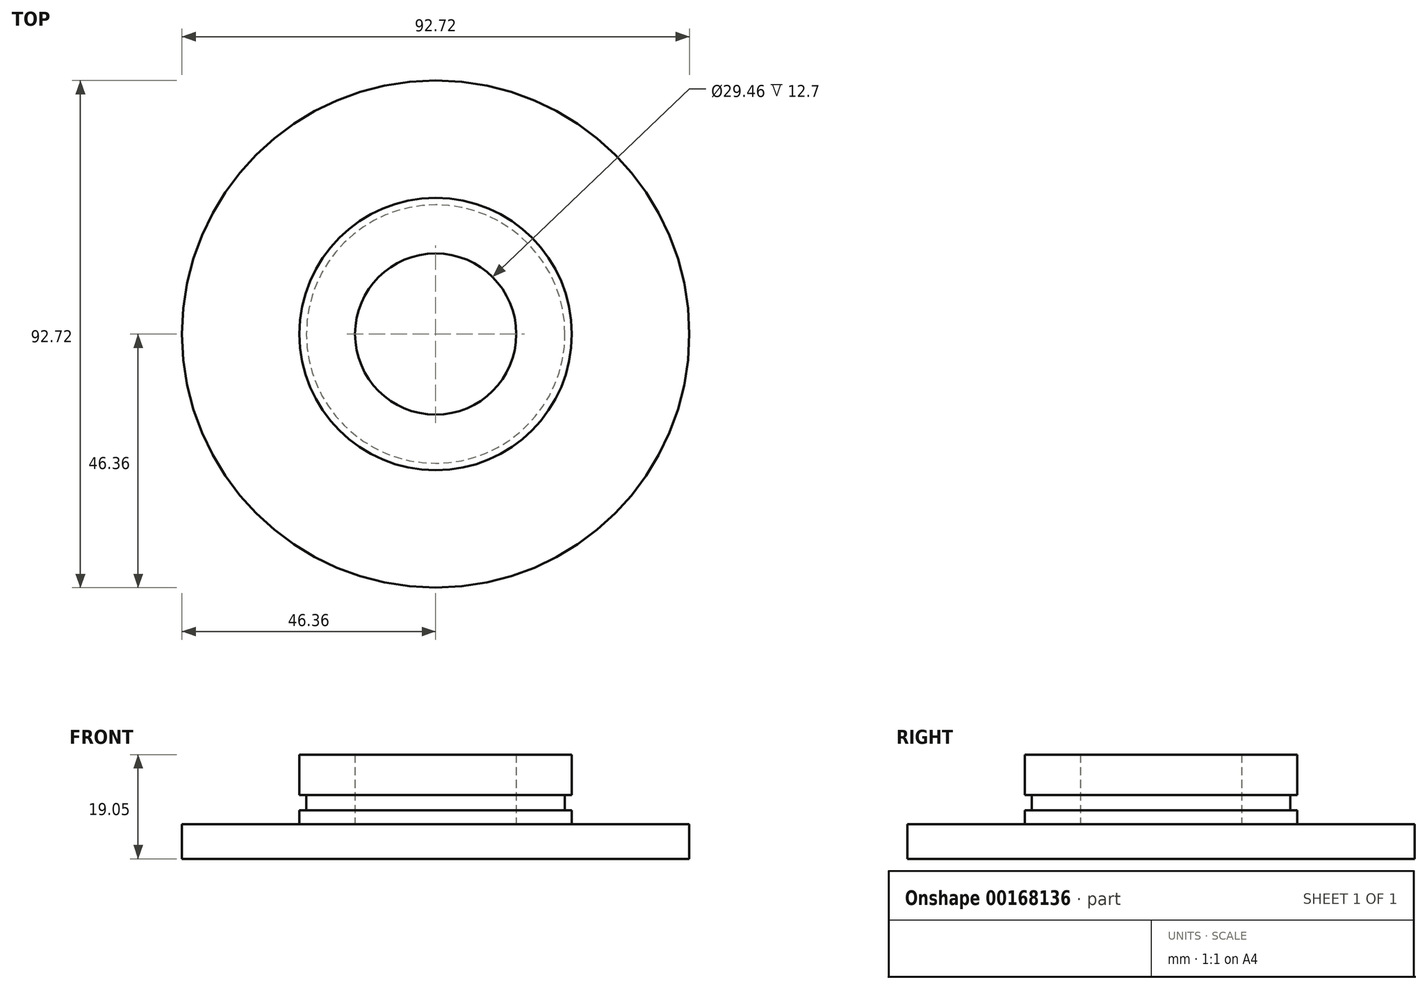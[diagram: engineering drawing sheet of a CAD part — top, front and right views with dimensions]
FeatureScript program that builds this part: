
annotation { "Feature Type Name" : "Feature", "Feature Type Description" : "" }
export const myFeature = defineFeature(function(context is Context, id is Id, definition is map)
    precondition{}
    {
        {
            var Q0;
            Q0=qCreatedBy(makeId("Top.planeOp"),FACE);
            var sketch = newSketch(context, id + "F0", { "sketchPlane" : qUnion([Q0])});
            skCircle(sketch, "E0", {"center": v(0, 0) * mm, "radius": 46.35 * mm});
            skSolve(sketch);
        }
        {
            var Q0;
            Q0=makeQuery(id+"F0.imprint","IMPRINT",FACE,{"disambiguationData":[TD([[makeQuery(id+"F0.imprint","IMPRINT",EDGE,{"derivedFrom":sQuery(id+"F0.wireOp",EDGE,"E0")}),1.0]])]});
            extrude(context, id + "F1", {"entities" : qUnion([Q0]), "depth" : 6.35 * mm});
        }
        {
            var Q0;
            Q0=makeQuery(id+"F1.opExtrude","CAP_FACE",FACE,{"disambiguationData":[OSD([sQuery(id+"F0.wireOp",EDGE,"E0")])],"isStart":false});
            var sketch = newSketch(context, id + "F2", { "sketchPlane" : qUnion([Q0])});
            skCircle(sketch, "E1", {"center": v(0, 0) * mm, "radius": 24.9 * mm});
            skCircle(sketch, "E2", {"center": v(0, 0) * mm, "radius": 14.73 * mm});
            skSolve(sketch);
        }
        {
            var Q0;
            Q0=qSketchRegion(id+"F2",true);
            extrude(context, id + "F3", {"entities" : qUnion([Q0]), "operationType" : NewBodyOperationType.ADD, "depth" : 12.7 * mm});
        }
        {
            var Q0;
            Q0=qCreatedBy(makeId("Front.planeOp"),FACE);
            var sketch = newSketch(context, id + "F4", { "sketchPlane" : qUnion([Q0])});
            skLineSegment(sketch, "E3.bottom", {"start": v(24.9, 8.9) * mm, "end": v(23.62, 8.9) * mm});
            skLineSegment(sketch, "E3.top", {"start": v(24.9, 11.68) * mm, "end": v(23.62, 11.68) * mm});
            skLineSegment(sketch, "E3.left", {"start": v(24.9, 8.9) * mm, "end": v(24.9, 11.68) * mm});
            skLineSegment(sketch, "E3.right", {"start": v(23.62, 8.9) * mm, "end": v(23.62, 11.68) * mm});
            skLineSegment(sketch, "E4", {"start": v(0, 0) * mm, "end": v(0, 8.9) * mm, "construction": true});
            skLineSegment(sketch, "E5", {"start": v(0, 8.9) * mm, "end": v(24.9, 8.9) * mm, "construction": true});
            skSolve(sketch);
        }
        {
            var Q0;
            Q0=qSketchRegion(id+"F4",true);
            var Q1;
            Q1=sQuery(id+"F4.wireOp",EDGE,"E4");
            revolve(context, id + "F5", {"operationType" : NewBodyOperationType.REMOVE, "entities" : qUnion([Q0]), "axis" : qUnion([Q1]), "revolveType" : RevolveType.FULL, "oppositeDirection" : true});
        }
        {
            var Q0;
            Q0=makeQuery(id+"F5.boolean.opBoolean","COPY",EDGE,{"derivedFrom":makeQuery(id+"F5.opRevolve","SWEPT_EDGE",EDGE,{"disambiguationData":[OSD([sQuery(id+"F4.wireOp",EDGE,"E3.top"),sQuery(id+"F4.wireOp",EDGE,"E3.right")])]})});
            var Q1;
            Q1=makeQuery(id+"F5.boolean.opBoolean","COPY",EDGE,{"derivedFrom":makeQuery(id+"F5.opRevolve","SWEPT_EDGE",EDGE,{"disambiguationData":[OSD([sQuery(id+"F4.wireOp",EDGE,"E3.bottom"),sQuery(id+"F4.wireOp",EDGE,"E3.right")])]})});
            fillet(context, id + "F6", {"entities" : qUnion([Q0, Q1]), "radius" : 0.25 * mm, "tangentPropagation" : true, "allowEdgeOverflow" : false});
        }
    });
